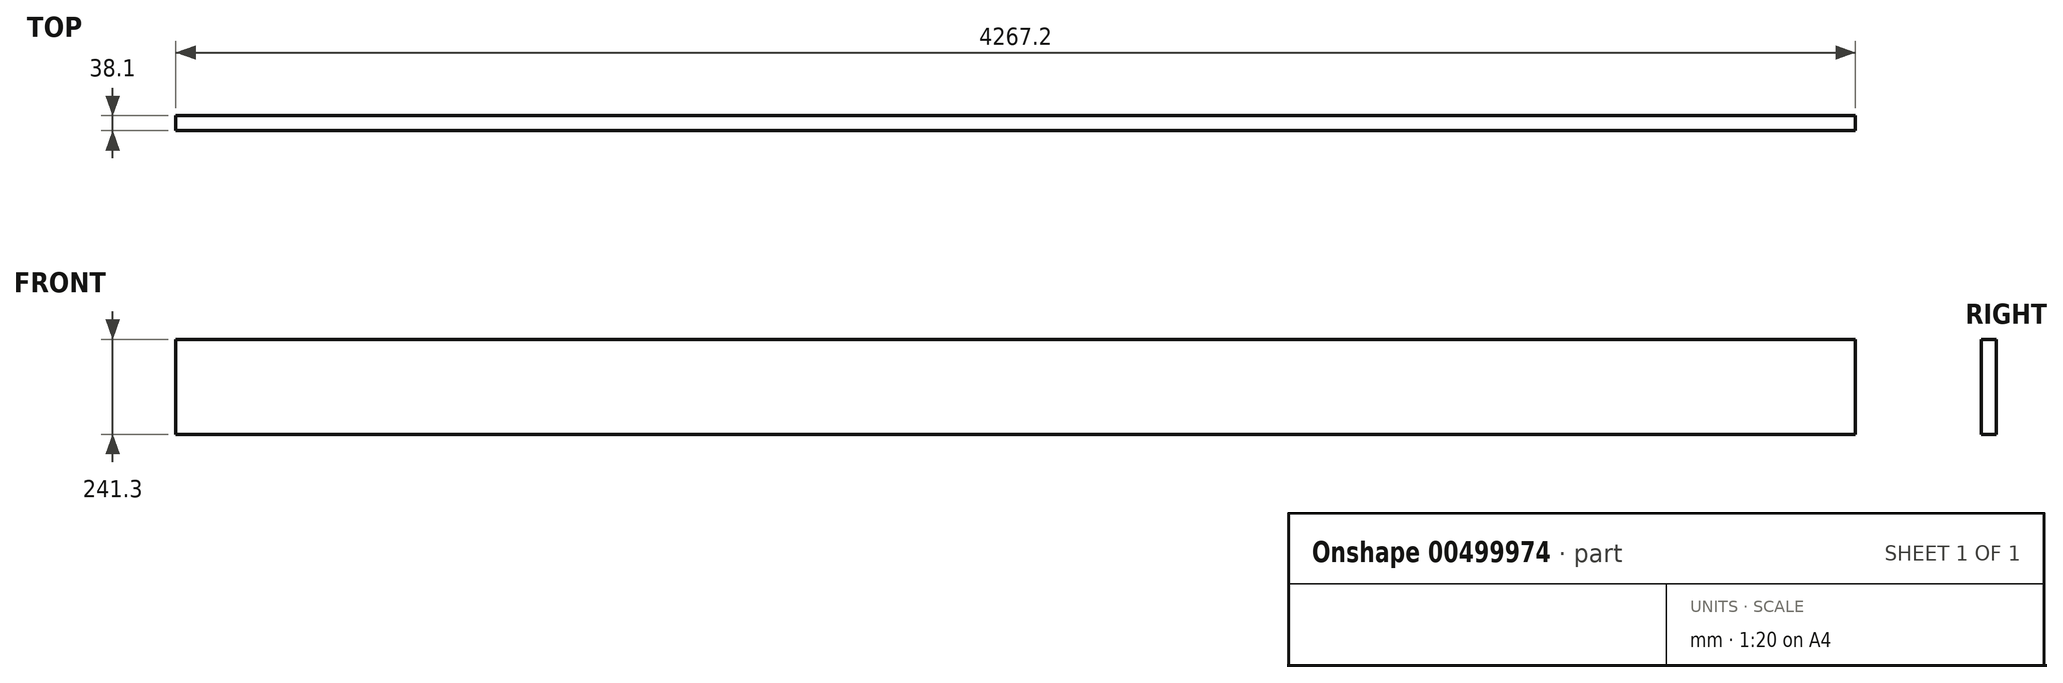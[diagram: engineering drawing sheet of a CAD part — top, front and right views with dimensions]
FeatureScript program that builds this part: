
annotation { "Feature Type Name" : "Feature", "Feature Type Description" : "" }
export const myFeature = defineFeature(function(context is Context, id is Id, definition is map)
    precondition{}
    {
        {
            var Q0;
            Q0=qCreatedBy(makeId("Front.planeOp"),FACE);
            var sketch = newSketch(context, id + "F0", { "sketchPlane" : qUnion([Q0])});
            skLineSegment(sketch, "E0.bottom", {"start": v(-2133.6, 120.65) * mm, "end": v(2133.6, 120.65) * mm});
            skLineSegment(sketch, "E0.top", {"start": v(-2133.6, -120.65) * mm, "end": v(2133.6, -120.65) * mm});
            skLineSegment(sketch, "E0.left", {"start": v(-2133.6, 120.65) * mm, "end": v(-2133.6, -120.65) * mm});
            skLineSegment(sketch, "E0.right", {"start": v(2133.6, 120.65) * mm, "end": v(2133.6, -120.65) * mm});
            skPoint(sketch, "E0.middle", {"position": v(0, 0) * mm});
            skSolve(sketch);
        }
        {
            var Q0;
            Q0 = qSketchRegion(id + "F0", true);
            extrude(context, id + "F1", {"entities" : qUnion([Q0]), "depth" : 38.1 * mm, "offsetDistance" : 25.4 * mm});
        }
    });
